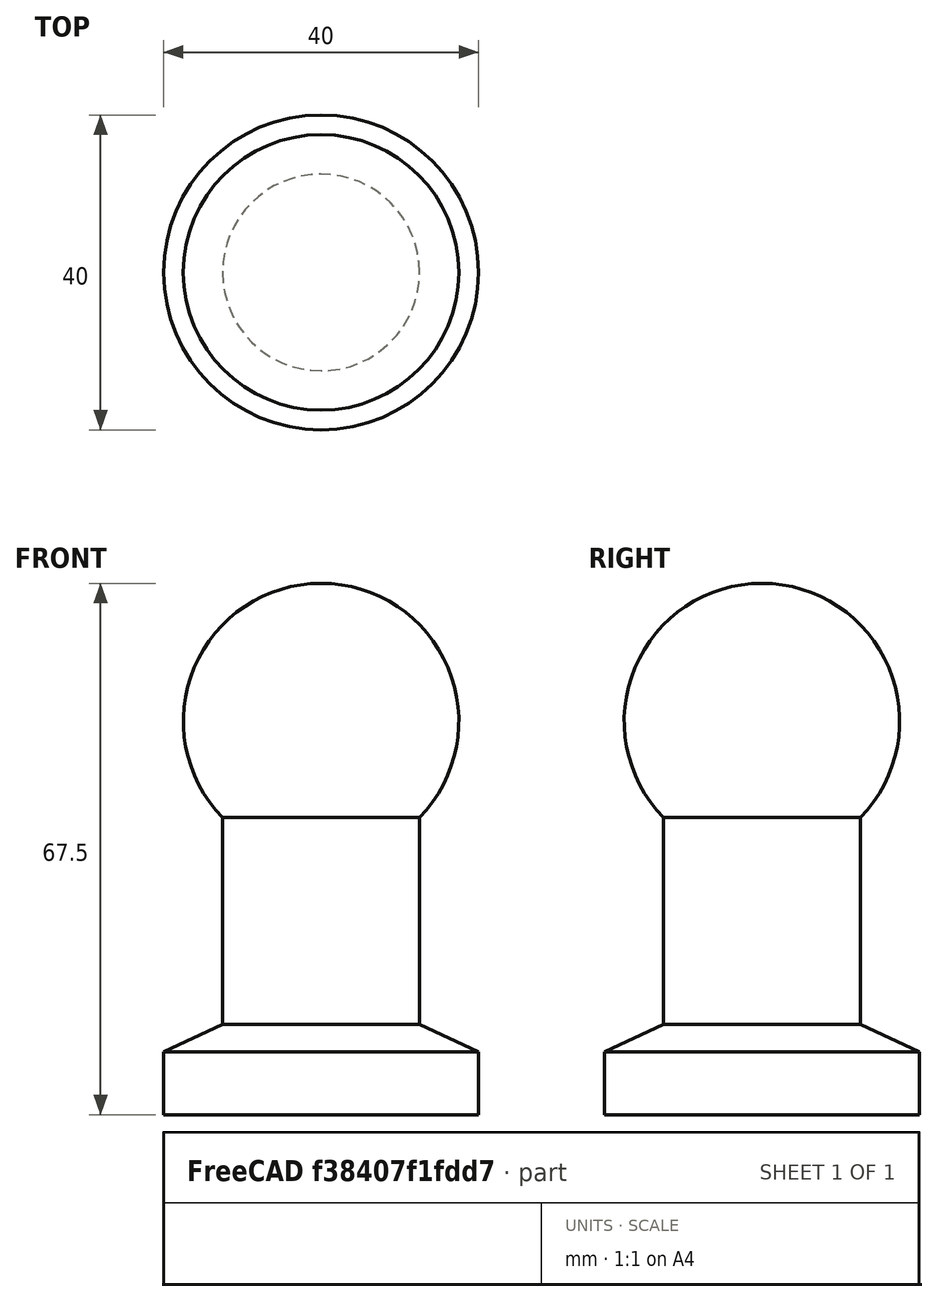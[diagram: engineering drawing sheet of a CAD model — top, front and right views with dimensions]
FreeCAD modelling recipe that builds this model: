
FCSTD DOCUMENT  (FreeCAD 1.1R44874 (Git))
Label: StampHolder
License: All rights reserved
LicenseURL: https://en.wikipedia.org/wiki/All_rights_reserved
objects: App::Point×1, Sketcher::SketchObject×1, PartDesign::Revolution×1, PartDesign::Body×1
note: 6 computed .brp shape members not serialized (recipe doc carries the construction recipe); baked Part::Feature solids carry a one-line shape summary decoded from their .brp

FEATURE [App::Point] Origin001
  Role = Origin
FEATURE [Sketcher::SketchObject] Sketch
  ArcFitTolerance = 1e-06
  AttachmentSupport = -> [Origin]
  ExternalTypes = [0]
  FullyConstrained = true
  MakeInternals = false
  MapMode = 5
  Placement = pos=(0,0,0) rot=(0.57735,0.57735,0.57735;2.0944rad)
  _ExternalGeoVersion = 1
  expr: Constraints[15] = 40 / 2
  expr: Constraints[16] = 25 / 2
  sketch-geometry (8):
    g0: LineSegment StartX=0 StartY=0 StartZ=0 EndX=20 EndY=0 EndZ=0
    g1: LineSegment StartX=20 StartY=0 StartZ=0 EndX=20 EndY=8 EndZ=0
    g2: LineSegment StartX=20 StartY=8 StartZ=0 EndX=12.5 EndY=11.4973 EndZ=0
    g3: LineSegment StartX=12.5 StartY=11.4973 StartZ=0 EndX=12.5 EndY=37.7526 EndZ=0
    g4: GeomPoint X=0 Y=67.5 Z=0
    g5: ArcOfCircle CenterX=0 CenterY=50 CenterZ=0 NormalX=0 NormalY=0 NormalZ=1 AngleXU=0 Radius=17.5 StartAngle=5.50799 EndAngle=7.85398
    g6: LineSegment [constr] StartX=0 StartY=67.5 StartZ=0 EndX=-10 EndY=67.5 EndZ=0
    g7: LineSegment StartX=0 StartY=67.5 StartZ=0 EndX=0 EndY=0 EndZ=0
  constraints (22):
    c: Coincident(g-1,g0)
    c: PointOnObject(g0,g-1)
    c: Coincident(g0,g1)
    c: Vertical(g1)
    c: Coincident(g1,g2)
    c: Coincident(g2,g3)
    c: Vertical(g3)
    c: PointOnObject(g4,g-2)
    c: PointOnObject(g5,g-2)
    c: Coincident(g5,g3)
    c: Coincident(g5,g4)
    c: Coincident(g6,g4)
    c: Horizontal(g6)
    c: Coincident(g7,g4)
    c: Coincident(g7,g0)
    c: DistanceX(g0,g0) = 20
    c: DistanceX(g0,g2) = 12.5
    c: DistanceY(g0,g5) = 50
    c: DistanceY(g1,g1) = 8
    c: Angle(g2,g1) = 2.00713
    c: Diameter(g5) = 35
    c: DistanceX(g6,g6) = 10
FEATURE [PartDesign::Revolution] Revolution
  Angle = 360
  Angle2 = 0
  Axis = (0,0,1)
  Base = (0,0,0)
  FuseOrder = 0
  Profile = -> Sketch
  ReferenceAxis = -> Sketch [V_Axis]
  Refine = true
  Reversed = true
  Suppressed = false
  Type = 0
FEATURE [PartDesign::Body] Body
  AllowCompound = true
  Group = -> [Sketch,Revolution]
  Origin = -> Origin
  Tip = -> Revolution
